# Revit family: Capsule Pool 600-1500 вытяжной
name_source: partatom
category: Оборудование
units: mm (PartAtom-declared; Revit-internal decimal feet)

## family parameters
Всегда вертикально = Да
Классификация = Нет
На основе рабочей плоскости = Нет
Общий = Нет
При загрузке вырезать с полостями = Нет
Размер круглого соединителя = Использовать диаметр
Тип детали = Нормальный
Точка расчета площади = Нет

## types (3) — shared parameters
ADSK_Единица измерения = шт.
ADSK_Завод-изготовитель = ООО «Турков»
ADSK_Наименование = Система климатизации бассейнов Capsule Pool вытяжной модуль
ADSK_Расход воздуха = 0.0 м³/ч
ВВ_высота = 27 мм
Крепеж_У = 23 мм
Крепеж_Х = 3 мм
Толщина_кр = 50 мм
zero-valued in all types: ADSK_Масса

## per-type parameters (varying)
| type | A1 длина | ADSK_Марка | B1 глубина | C1 высота | D_вытяж | D_приток | ВВ_выт_Y | ВВ_прит_X | СЗ |
| Capsule Pool 600 | 530 мм | Capsule Pool 600 v | 337 мм | 556 мм | 200 мм | 160 мм | 165 мм | 230 мм | 283 мм |
| Capsule Pool 1000 | 528 мм | Capsule Pool 1000 | 387 мм | 556 мм | 250 мм | 200 мм | 225 мм | 264 мм | 300 мм |
| Capsule Pool 1500 | 528 мм | Capsule Pool 1500 | 437 мм | 656 мм | 315 мм | 250 мм | 250 мм | 264 мм | 300 мм |
